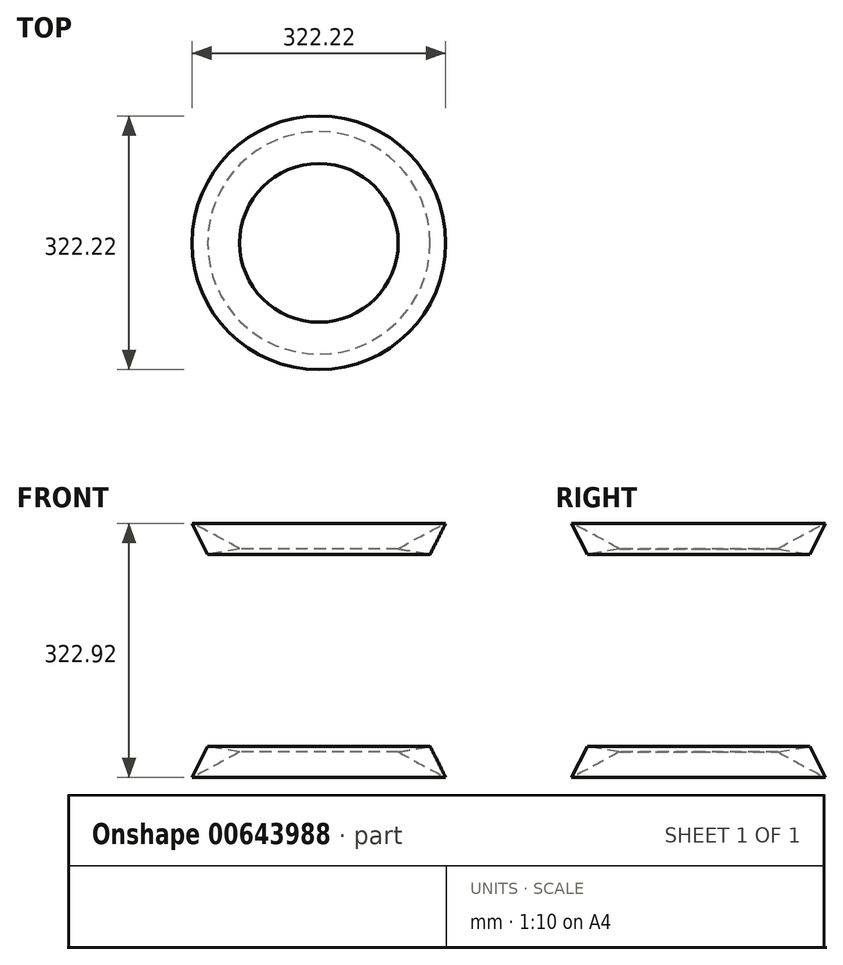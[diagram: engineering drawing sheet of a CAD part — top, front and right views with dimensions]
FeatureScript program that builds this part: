
annotation { "Feature Type Name" : "Feature", "Feature Type Description" : "" }
export const myFeature = defineFeature(function(context is Context, id is Id, definition is map)
    precondition{}
    {
        {
            var Q0;
            Q0=qCreatedBy(makeId("Front.planeOp"),FACE);
            var sketch = newSketch(context, id + "F0", { "sketchPlane" : qUnion([Q0])});
            skLineSegment(sketch, "E0", {"start": v(0, -40.91) * mm, "end": v(0, -59.86) * mm, "construction": true});
            skLineSegment(sketch, "E1", {"start": v(0, -59.86) * mm, "end": v(-161.1, -59.86) * mm, "construction": true});
            skLineSegment(sketch, "E2", {"start": v(0, -40.91) * mm, "end": v(0, -27.4) * mm, "construction": true});
            skLineSegment(sketch, "E3", {"start": v(0, -27.4) * mm, "end": v(-100.76, -27.4) * mm, "construction": true});
            skLineSegment(sketch, "E4", {"start": v(0, -40.91) * mm, "end": v(0, -20.46) * mm, "construction": true});
            skPoint(sketch, "E4.endSnap0", {"position": v(0, -34.15) * mm});
            skLineSegment(sketch, "E5", {"start": v(0, -20.46) * mm, "end": v(-141.3, -20.46) * mm, "construction": true});
            skLineSegment(sketch, "E6", {"start": v(-100.76, -27.4) * mm, "end": v(-141.3, -20.46) * mm});
            skLineSegment(sketch, "E7", {"start": v(-141.3, -20.46) * mm, "end": v(-161.1, -59.86) * mm});
            skArc(sketch, "E8", {"start": v(-161.1, -59.86) * mm, "mid": v(-130.75, -43.97) * mm, "end": v(-100.76, -27.4) * mm});
            skSolve(sketch);
        }
        {
            var Q0;
            Q0=qSketchRegion(id+"F0",true);
            var Q1;
            Q1=sQuery(id+"F0.wireOp",EDGE,"E0");
            revolve(context, id + "F1", {"entities" : qUnion([Q0]), "axis" : qUnion([Q1]), "revolveType" : RevolveType.SYMMETRIC, "angle" : 360 * degree});
        }
        {
            var Q0;
            Q0=qCreatedBy(makeId("Top.planeOp"),FACE);
            cPlane(context, id + "F2", {"entities" : qUnion([Q0]), "cplaneType" : CPlaneType.OFFSET, "offset" : 101.6 * mm, "width" : 152.4 * mm, "height" : 152.4 * mm});
        }
        {
            var Q0;
            Q0=makeQuery(id+"F1.opRevolve","SWEPT_BODY",BODY,{"disambiguationData":[OSD([sQuery(id+"F0.wireOp",EDGE,"E6"),sQuery(id+"F0.wireOp",EDGE,"E7"),sQuery(id+"F0.wireOp",EDGE,"E8")])]});
            var Q1;
            Q1=qCreatedBy(id+"F2.planeOp",FACE);
            mirror(context, id + "F3", {"entities" : qUnion([Q0]), "mirrorPlane" : qUnion([Q1])});
        }
    });
